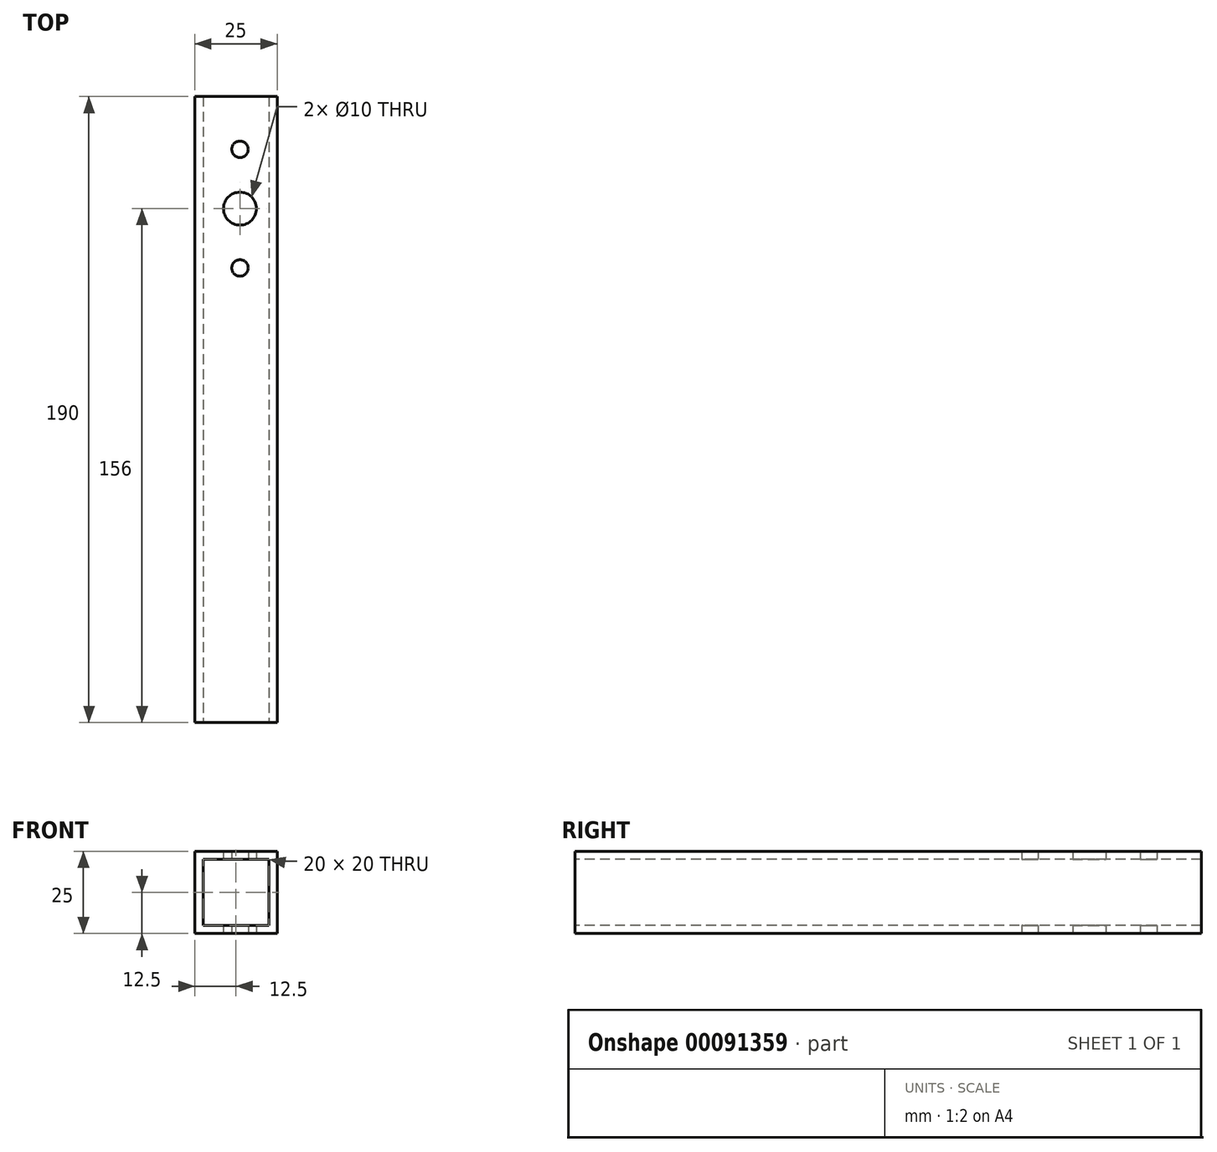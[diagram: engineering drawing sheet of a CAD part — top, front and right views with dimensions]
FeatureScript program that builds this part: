
annotation { "Feature Type Name" : "Feature", "Feature Type Description" : "" }
export const myFeature = defineFeature(function(context is Context, id is Id, definition is map)
    precondition{}
    {
        {
            var Q0;
            Q0=qCreatedBy(makeId("Front.planeOp"),FACE);
            var sketch = newSketch(context, id + "F0", { "sketchPlane" : qUnion([Q0])});
            skLineSegment(sketch, "E0.bottom", {"start": v(0, 0) * mm, "end": v(25, 0) * mm});
            skLineSegment(sketch, "E0.top", {"start": v(0, 25) * mm, "end": v(25, 25) * mm});
            skLineSegment(sketch, "E0.left", {"start": v(0, 0) * mm, "end": v(0, 25) * mm});
            skLineSegment(sketch, "E0.right", {"start": v(25, 0) * mm, "end": v(25, 25) * mm});
            skSolve(sketch);
        }
        {
            var Q0;
            Q0=makeQuery(id+"F0.imprint","IMPRINT",FACE,{"disambiguationData":[TD([[makeQuery(id+"F0.imprint","IMPRINT",EDGE,{"derivedFrom":sQuery(id+"F0.wireOp",EDGE,"E0.bottom")}),1.0]])]});
            extrude(context, id + "F1", {"entities" : qUnion([Q0]), "oppositeDirection" : true, "depth" : 190 * mm});
        }
        {
            var Q0;
            Q0=makeQuery(id+"F1.opExtrude","CAP_FACE",FACE,{"disambiguationData":[OSD([sQuery(id+"F0.wireOp",EDGE,"E0.bottom"),sQuery(id+"F0.wireOp",EDGE,"E0.top"),sQuery(id+"F0.wireOp",EDGE,"E0.left"),sQuery(id+"F0.wireOp",EDGE,"E0.right")])],"isStart":true});
            var Q1;
            Q1=makeQuery(id+"F1.opExtrude","CAP_FACE",FACE,{"disambiguationData":[OSD([sQuery(id+"F0.wireOp",EDGE,"E0.bottom"),sQuery(id+"F0.wireOp",EDGE,"E0.top"),sQuery(id+"F0.wireOp",EDGE,"E0.left"),sQuery(id+"F0.wireOp",EDGE,"E0.right")])],"isStart":false});
            shell(context, id + "F2", {"entities" : qUnion([Q0, Q1]), "thickness" : 2.5 * mm});
        }
        {
            var Q0;
            Q0=makeQuery(id+"F1.opExtrude","SWEPT_FACE",FACE,{"disambiguationData":[OSD([sQuery(id+"F0.wireOp",EDGE,"E0.top")])]});
            var sketch = newSketch(context, id + "F3", { "sketchPlane" : qUnion([Q0])});
            skLineSegment(sketch, "E1", {"start": v(0, 20.54) * mm, "end": v(0, 0) * mm, "construction": true});
            skPoint(sketch, "E2", {"position": v(13.7, 156) * mm});
            skPoint(sketch, "E3", {"position": v(13.7, 174) * mm});
            skPoint(sketch, "E4", {"position": v(13.7, 138) * mm});
            skSolve(sketch);
        }
        {
            var Q0;
            Q0=sQuery(id+"F3.wireOp",VERTEX,"E2");
            var Q1;
            Q1=makeQuery(id+"F1.opExtrude","SWEPT_BODY",BODY,{"disambiguationData":[OSD([sQuery(id+"F0.wireOp",EDGE,"E0.bottom"),sQuery(id+"F0.wireOp",EDGE,"E0.top"),sQuery(id+"F0.wireOp",EDGE,"E0.left"),sQuery(id+"F0.wireOp",EDGE,"E0.right")])]});
            hole(context, id + "F4", {"style" : HoleStyle.SIMPLE, "endStyle" : HoleEndStyle.THROUGH, "standardTappedOrClearance" : lookupTablePath({ "standard" : "ISO", "size" : "10", "type" : "Drilled" }), "standardBlindInLast" : lookupTablePath({ "standard" : "ISO", "size" : "10", "type" : "Drilled" }), "holeDiameter" : 10 * mm, "locations" : qUnion([Q0]), "scope" : qUnion([Q1]), "isTappedThrough" : true, "startStyle" : HoleStartStyle.SKETCH});
        }
        {
            var Q0;
            Q0=sQuery(id+"F3.wireOp",VERTEX,"E4");
            var Q1;
            Q1=sQuery(id+"F3.wireOp",VERTEX,"E3");
            var Q2;
            Q2=makeQuery(id+"F1.opExtrude","SWEPT_BODY",BODY,{"disambiguationData":[OSD([sQuery(id+"F0.wireOp",EDGE,"E0.bottom"),sQuery(id+"F0.wireOp",EDGE,"E0.top"),sQuery(id+"F0.wireOp",EDGE,"E0.left"),sQuery(id+"F0.wireOp",EDGE,"E0.right")])]});
            hole(context, id + "F5", {"style" : HoleStyle.SIMPLE, "endStyle" : HoleEndStyle.THROUGH, "standardTappedOrClearance" : lookupTablePath({ "standard" : "ISO", "size" : "5", "type" : "Drilled" }), "standardBlindInLast" : lookupTablePath({ "standard" : "ISO", "size" : "5", "type" : "Drilled" }), "holeDiameter" : 5 * mm, "locations" : qUnion([Q0, Q1]), "scope" : qUnion([Q2]), "isTappedThrough" : true, "startStyle" : HoleStartStyle.SKETCH});
        }
    });
